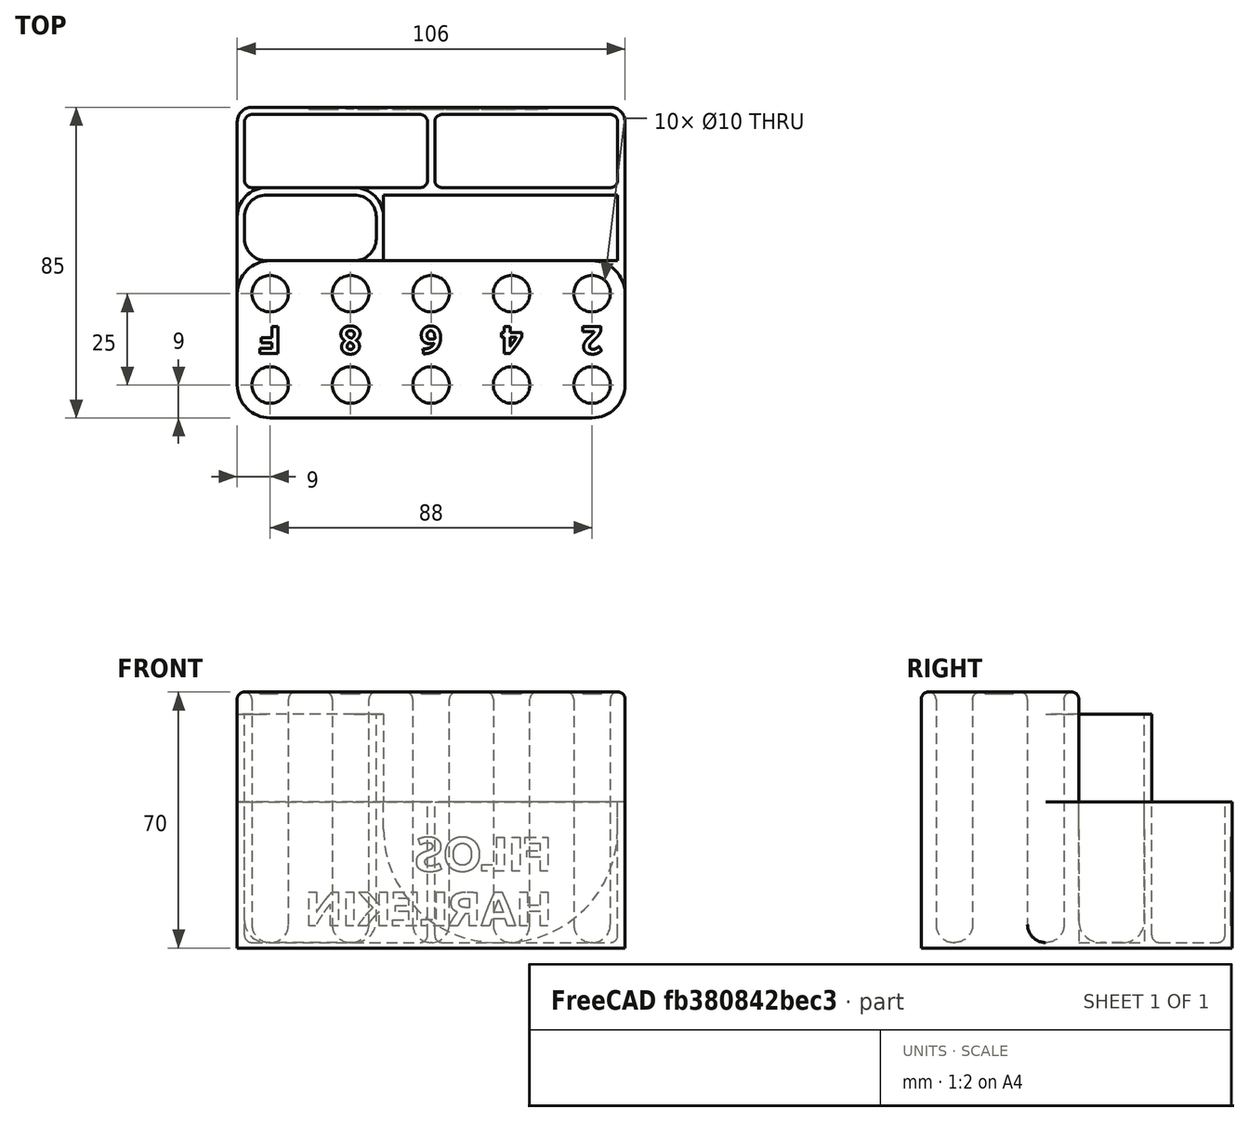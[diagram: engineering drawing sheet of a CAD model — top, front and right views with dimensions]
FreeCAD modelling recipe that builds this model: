
FCSTD DOCUMENT  (FreeCAD 0.21R33771 (Git))
Label: DrawingKitStand
License: All rights reserved
LicenseURL: https://en.wikipedia.org/wiki/All_rights_reserved
objects: Part::Fillet×11, Part::Feature×9, Part::Box×7, Part::Part2DObjectPython×7, Part::Extrusion×7, Part::MultiFuse×4, Part::Cut×3, Part::Cylinder×1
note: 49 computed .brp shape members not serialized (recipe doc carries the construction recipe); baked Part::Feature solids carry a one-line shape summary decoded from their .brp

FEATURE [Part::Cylinder] Cylinder
  Angle = 360
  AttacherType = Attacher::AttachEngine3D
  FirstAngle = 0
  Height = 70
  Placement = pos=(0,0,1.5) rot=(0,0,1;0rad)
  Radius = 5
  SecondAngle = 0
FEATURE [Part::Fillet] Fillet  label="PencilHolle001"
  Base = -> Cylinder
  Edges = 1 edges r=4.9: [Edge2]
FEATURE [Part::Feature] Fillet001  label="PencilHolle002"
  Placement = pos=(22,0,0) rot=(0,0,1;0rad)
  shape: bbox 10 x 10 x 70 mm, 4 faces (baked)
FEATURE [Part::Feature] Fillet002  label="PencilHolle003"
  Placement = pos=(44,0,0) rot=(0,0,1;0rad)
  shape: bbox 10 x 10 x 70 mm, 4 faces (baked)
FEATURE [Part::Feature] Fillet003  label="PencilHolle004"
  Placement = pos=(66,0,0) rot=(0,0,1;0rad)
  shape: bbox 10 x 10 x 70 mm, 4 faces (baked)
FEATURE [Part::Feature] Fillet004  label="PencilHolle005"
  Placement = pos=(88,0,0) rot=(0,0,1;0rad)
  shape: bbox 10 x 10 x 70 mm, 4 faces (baked)
FEATURE [Part::Feature] Fillet006  label="PencilHolle007"
  Placement = pos=(0,25,0) rot=(0,0,1;0rad)
  shape: bbox 10 x 10 x 70 mm, 4 faces (baked)
FEATURE [Part::Feature] Fillet007  label="PencilHolle008"
  Placement = pos=(22,25,0) rot=(0,0,1;0rad)
  shape: bbox 10 x 10 x 70 mm, 4 faces (baked)
FEATURE [Part::Feature] Fillet008  label="PencilHolle009"
  Placement = pos=(44,25,0) rot=(0,0,1;0rad)
  shape: bbox 10 x 10 x 70 mm, 4 faces (baked)
FEATURE [Part::Feature] Fillet009  label="PencilHolle010"
  Placement = pos=(66,25,0) rot=(0,0,1;0rad)
  shape: bbox 10 x 10 x 70 mm, 4 faces (baked)
FEATURE [Part::Feature] Fillet010  label="PencilHolle011"
  Placement = pos=(88,25,0) rot=(0,0,1;0rad)
  shape: bbox 10 x 10 x 70 mm, 4 faces (baked)
FEATURE [Part::Box] Box  label="Cube"
  AttacherType = Attacher::AttachEngine3D
  Height = 40
  Length = 64
  Placement = pos=(31,34,1.5) rot=(0,0,1;0rad)
  Width = 18
FEATURE [Part::Fillet] Fillet011
  Base = -> Box
  Edges = 2 edges r=31: [Edge4,Edge8]
FEATURE [Part::Box] Box001  label="Cube001"
  AttacherType = Attacher::AttachEngine3D
  Height = 40
  Length = 50
  Placement = pos=(-7,54,1.5) rot=(0,0,1;0rad)
  Width = 20
FEATURE [Part::Box] Box002  label="Cube002"
  AttacherType = Attacher::AttachEngine3D
  Height = 40
  Length = 50
  Placement = pos=(45,54,1.5) rot=(0,0,1;0rad)
  Width = 20
FEATURE [Part::Fillet] Fillet012
  Base = -> Box002
  Edges = 8 edges r=2: [Edge1,Edge3,Edge4,Edge5,Edge7,Edge8,Edge9,Edge11]
FEATURE [Part::Fillet] Fillet013
  Base = -> Box001
  Edges = 8 edges r=2: [Edge1,Edge3,Edge4,Edge5,Edge7,Edge8,Edge9,Edge11]
FEATURE [Part::Box] Box003  label="Cube003"
  AttacherType = Attacher::AttachEngine3D
  Height = 70
  Length = 106
  Placement = pos=(-9,-9,0) rot=(0,0,1;0rad)
  Width = 43
FEATURE [Part::Box] Box004  label="Cube004"
  AttacherType = Attacher::AttachEngine3D
  Height = 70
  Length = 36
  Placement = pos=(-7,34,1.5) rot=(0,0,1;0rad)
  Width = 18
FEATURE [Part::Fillet] Fillet015
  Base = -> Box003
  Edges = 4 edges r=9: [Edge1,Edge3,Edge5,Edge7]
FEATURE [Part::Box] Box005  label="Cube005"
  AttacherType = Attacher::AttachEngine3D
  Height = 64
  Length = 40
  Placement = pos=(-9,20,0) rot=(0,0,1;0rad)
  Width = 34
FEATURE [Part::Fillet] Fillet016
  Base = -> Box005
  Edges = 2 edges r=8: [Edge3,Edge7]
FEATURE [Part::Fillet] Fillet017
  Base = -> Box004
  Edges = 4 edges r=6: [Edge1,Edge3,Edge5,Edge7]
FEATURE [Part::Fillet] Fillet018
  Base = -> Fillet017
  Edges = 1 edges r=6: [Edge3]
FEATURE [Part::Box] Box006  label="Cube006"
  AttacherType = Attacher::AttachEngine3D
  Height = 40
  Length = 106
  Placement = pos=(-9,20,0) rot=(0,0,1;0rad)
  Width = 56
FEATURE [Part::Fillet] Fillet019
  Base = -> Box006
  Edges = 2 edges r=4: [Edge3,Edge7]
FEATURE [Part::MultiFuse] Fusion  label="Hollows"
  Shapes = -> [Fillet018,Fillet,Fillet001,Fillet002,Fillet003,Fillet004,Fillet006,Fillet007,Fillet008,Fillet009,Fillet010,Fillet011,Fillet012,Fillet013]
FEATURE [Part::MultiFuse] Fusion001  label="Body"
  Shapes = -> [Fillet015,Fillet016,Fillet019]
FEATURE [Part::Cut] Cut
  Base = -> Fusion001
  Tool = -> Fusion
FEATURE [Part::Fillet] Fillet020
  Base = -> Cut
  Edges = 10 edges r=2: [Edge16,Edge17,Edge18,Edge19,Edge20,Edge21,Edge22,Edge23,Edge24,Edge25]
FEATURE [Part::Fillet] Fillet021
  Base = -> Fillet020
  Edges = 1 edges r=1.8: [Edge8]
FEATURE [Part::Part2DObjectPython] ShapeString  # Draft 2D object (typed FeaturePython)
  FontFile = <userpath>/Projects/3D-Print-models/Ubuntu-B.ttf
  MakeFace = true
  Placement = pos=(-3,9,0) rot=(0,0,1;0rad)
  Size = 4
  String = 2
  Tracking = 0
FEATURE [Part::Extrusion] Extrude
  Base = -> ShapeString
  Dir = (0,0,1)
  DirMode = 2
  FaceMakerClass = Part::FaceMakerBullseye
  LengthFwd = 1
  LengthRev = 0
  Placement = pos=(0,0,69.5) rot=(0,0,1;0rad)
  Solid = false
  Symmetric = false
FEATURE [Part::Part2DObjectPython] ShapeString001  # Draft 2D object (typed FeaturePython)
  FontFile = <userpath>/Projects/3D-Print-models/Ubuntu-B.ttf
  MakeFace = true
  Placement = pos=(19,9,0) rot=(0,0,1;0rad)
  Size = 4
  String = 4
  Tracking = 0
FEATURE [Part::Extrusion] Extrude001
  Base = -> ShapeString001
  Dir = (0,0,1)
  DirMode = 2
  FaceMakerClass = Part::FaceMakerBullseye
  LengthFwd = 1
  LengthRev = 0
  Placement = pos=(0,0,69.5) rot=(0,0,1;0rad)
  Solid = false
  Symmetric = false
FEATURE [Part::Part2DObjectPython] ShapeString002  # Draft 2D object (typed FeaturePython)
  FontFile = <userpath>/Projects/3D-Print-models/Ubuntu-B.ttf
  MakeFace = true
  Placement = pos=(41,9,0) rot=(0,0,1;0rad)
  Size = 4
  String = 6
  Tracking = 0
FEATURE [Part::Extrusion] Extrude002
  Base = -> ShapeString002
  Dir = (0,0,1)
  DirMode = 2
  FaceMakerClass = Part::FaceMakerBullseye
  LengthFwd = 1
  LengthRev = 0
  Placement = pos=(0,0,69.5) rot=(0,0,1;0rad)
  Solid = false
  Symmetric = false
FEATURE [Part::Part2DObjectPython] ShapeString003  # Draft 2D object (typed FeaturePython)
  FontFile = <userpath>/Projects/3D-Print-models/Ubuntu-B.ttf
  MakeFace = true
  Placement = pos=(63,9,0) rot=(0,0,1;0rad)
  Size = 4
  String = 8
  Tracking = 0
FEATURE [Part::Extrusion] Extrude003
  Base = -> ShapeString003
  Dir = (0,0,1)
  DirMode = 2
  FaceMakerClass = Part::FaceMakerBullseye
  LengthFwd = 1
  LengthRev = 0
  Placement = pos=(0,0,69.5) rot=(0,0,1;0rad)
  Solid = false
  Symmetric = false
FEATURE [Part::Part2DObjectPython] ShapeString004  # Draft 2D object (typed FeaturePython)
  FontFile = <userpath>/Projects/3D-Print-models/Ubuntu-B.ttf
  MakeFace = true
  Placement = pos=(85,9,0) rot=(0,0,1;0rad)
  Size = 4
  String = F
  Tracking = 0
FEATURE [Part::Extrusion] Extrude004
  Base = -> ShapeString004
  Dir = (0,0,1)
  DirMode = 2
  FaceMakerClass = Part::FaceMakerBullseye
  LengthFwd = 1
  LengthRev = 0
  Placement = pos=(0,0,69.5) rot=(0,0,1;0rad)
  Solid = false
  Symmetric = false
FEATURE [Part::MultiFuse] Fusion002  label="Markings"
  Placement = pos=(88,25,0) rot=(0,0,1;3.14159rad)
  Shapes = -> [Extrude004,Extrude003,Extrude002,Extrude001,Extrude]
FEATURE [Part::Cut] Cut001
  Base = -> Fillet021
  Tool = -> Fusion002
FEATURE [Part::Part2DObjectPython] ShapeString005  # Draft 2D object (typed FeaturePython)
  FontFile = <userpath>/Projects/3D-Print-models/Ubuntu-B.ttf
  MakeFace = true
  Placement = pos=(-3,9,0) rot=(0,0,1;3.14159rad)
  Size = 5
  String = FILOS
  Tracking = 0
FEATURE [Part::Extrusion] Extrude005
  Base = -> ShapeString005
  Dir = (0,0,1)
  DirMode = 2
  FaceMakerClass = Part::FaceMakerBullseye
  LengthFwd = 1
  LengthRev = 0
  Placement = pos=(80,75.5,30) rot=(1,0,0;-1.5708rad)
  Solid = false
  Symmetric = false
FEATURE [Part::Part2DObjectPython] ShapeString006  # Draft 2D object (typed FeaturePython)
  FontFile = <userpath>/Projects/3D-Print-models/Ubuntu-B.ttf
  MakeFace = true
  Placement = pos=(-3,9,0) rot=(0,0,1;3.14159rad)
  Size = 5
  String = HARLEKIN
  Tracking = 0
FEATURE [Part::Extrusion] Extrude006
  Base = -> ShapeString006
  Dir = (0,0,1)
  DirMode = 2
  FaceMakerClass = Part::FaceMakerBullseye
  LengthFwd = 1
  LengthRev = 0
  Placement = pos=(80,75.5,15) rot=(-1,0,0;1.5708rad)
  Solid = false
  Symmetric = false
FEATURE [Part::MultiFuse] Fusion003  label="NameTag"
  Shapes = -> [Extrude005,Extrude006]
FEATURE [Part::Cut] Cut002
  Base = -> Cut001
  Tool = -> Fusion003
